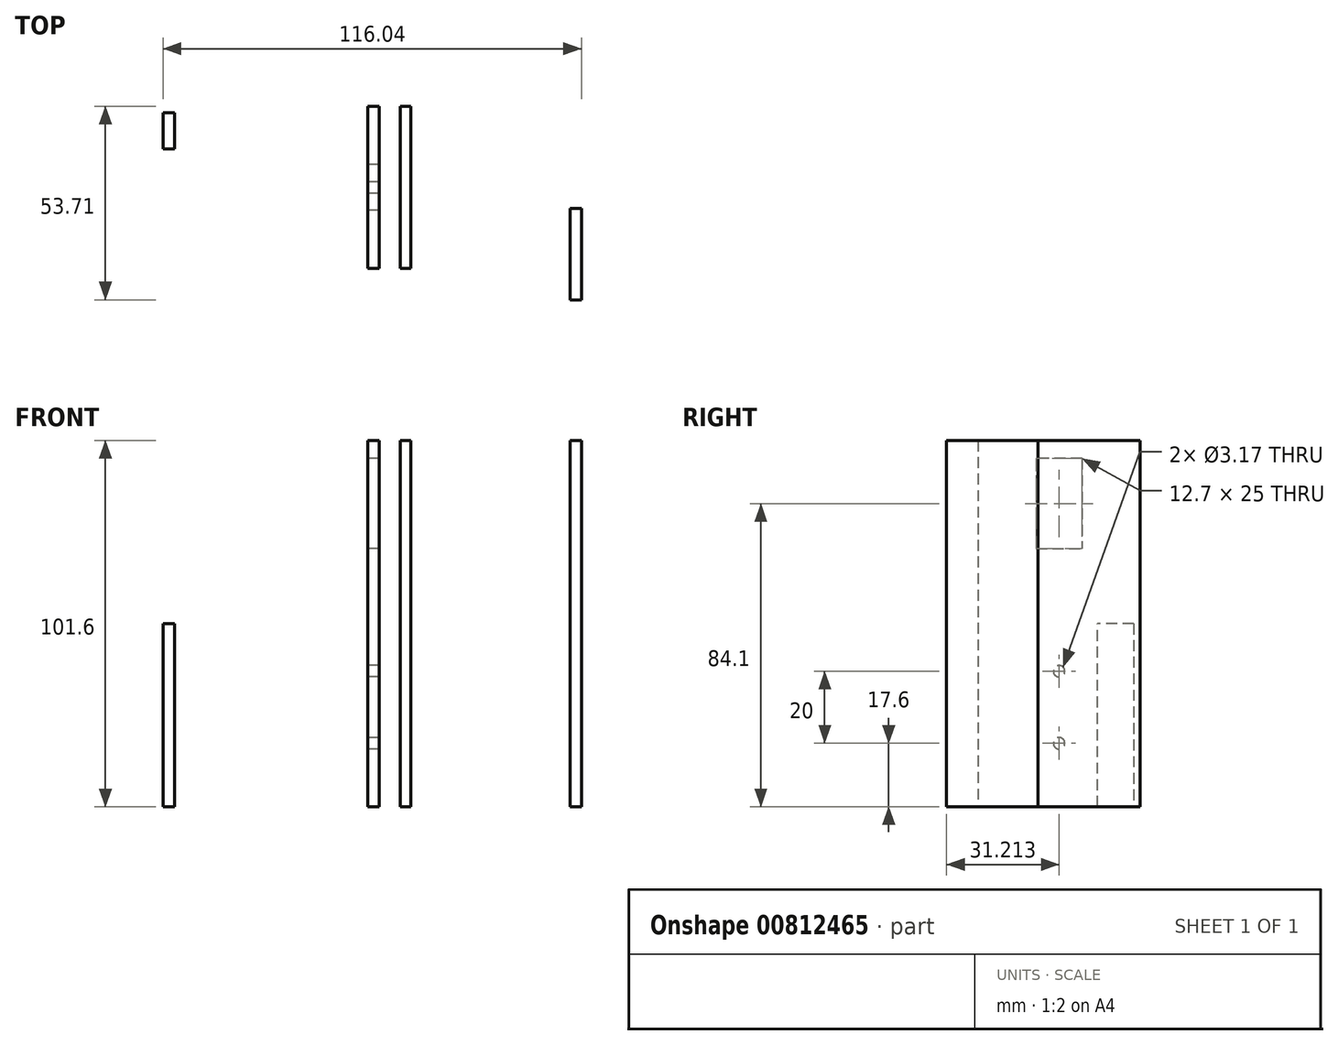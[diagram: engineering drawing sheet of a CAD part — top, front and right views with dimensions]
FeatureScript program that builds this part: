
annotation { "Feature Type Name" : "Feature", "Feature Type Description" : "" }
export const myFeature = defineFeature(function(context is Context, id is Id, definition is map)
    precondition{}
    {
        {
            var Q0;
            Q0=qCreatedBy(makeId("Top.planeOp"),FACE);
            var sketch = newSketch(context, id + "F0", { "sketchPlane" : qUnion([Q0])});
            skLineSegment(sketch, "E0.bottom", {"start": v(-7.16, 39.12) * mm, "end": v(-3.99, 39.12) * mm});
            skLineSegment(sketch, "E0.top", {"start": v(-7.16, -5.88) * mm, "end": v(-3.99, -5.88) * mm});
            skLineSegment(sketch, "E0.left", {"start": v(-7.16, 39.12) * mm, "end": v(-7.16, -5.88) * mm});
            skLineSegment(sketch, "E0.right", {"start": v(-3.99, 39.12) * mm, "end": v(-3.99, -5.88) * mm});
            skLineSegment(sketch, "E1.bottom", {"start": v(1.92, 39.12) * mm, "end": v(4.75, 39.12) * mm});
            skLineSegment(sketch, "E1.top", {"start": v(1.92, -5.88) * mm, "end": v(4.75, -5.88) * mm});
            skLineSegment(sketch, "E1.left", {"start": v(1.92, 39.12) * mm, "end": v(1.92, -5.88) * mm});
            skLineSegment(sketch, "E1.right", {"start": v(4.75, 39.12) * mm, "end": v(4.75, -5.88) * mm});
            skLineSegment(sketch, "E2", {"start": v(-63.9, 37.32) * mm, "end": v(-60.73, 37.32) * mm});
            skLineSegment(sketch, "E3", {"start": v(-60.73, 37.32) * mm, "end": v(-60.73, 17.32) * mm});
            skLineSegment(sketch, "E4.bottom", {"start": v(-60.73, 37.32) * mm, "end": v(-63.9, 37.32) * mm});
            skLineSegment(sketch, "E4.top", {"start": v(-60.73, 17.32) * mm, "end": v(-63.9, 17.32) * mm});
            skLineSegment(sketch, "E4.right", {"start": v(-63.9, 37.32) * mm, "end": v(-63.9, 17.32) * mm});
            skLineSegment(sketch, "E5", {"start": v(-62.32, 37.32) * mm, "end": v(-62.32, 17.32) * mm});
            skLineSegment(sketch, "E6", {"start": v(-63.9, 37.32) * mm, "end": v(-63.9, 27.32) * mm});
            skLineSegment(sketch, "E7.bottom", {"start": v(48.96, 10.81) * mm, "end": v(52.13, 10.81) * mm});
            skLineSegment(sketch, "E7.top", {"start": v(48.96, -14.59) * mm, "end": v(52.13, -14.59) * mm});
            skLineSegment(sketch, "E7.left", {"start": v(48.96, 10.81) * mm, "end": v(48.96, -14.59) * mm});
            skLineSegment(sketch, "E7.right", {"start": v(52.13, 10.81) * mm, "end": v(52.13, -14.59) * mm});
            skSolve(sketch);
        }
        {
            var Q0;
            Q0=makeQuery(id+"F0.imprint","IMPRINT",FACE,{"disambiguationData":[TD([[makeQuery(id+"F0.imprint","IMPRINT",EDGE,{"derivedFrom":sQuery(id+"F0.wireOp",EDGE,"E1.bottom")}),-1.0]])]});
            var Q1;
            Q1=makeQuery(id+"F0.imprint","IMPRINT",FACE,{"disambiguationData":[TD([[makeQuery(id+"F0.imprint","IMPRINT",EDGE,{"derivedFrom":sQuery(id+"F0.wireOp",EDGE,"E0.bottom")}),-1.0]])]});
            var Q2;
            {var subQ0=sQuery(id+"F0.wireOp",EDGE,"E3");Q2=makeQuery(id+"F0.imprint","IMPRINT",FACE,{"disambiguationData":[TD([[makeQuery(id+"F0.imprint","IMPRINT",EDGE,{"derivedFrom":subQ0}),-1.0]])]});}
            var Q3;
            {var subQ0=sQuery(id+"F0.wireOp",EDGE,"E4.right");Q3=makeQuery(id+"F0.imprint","IMPRINT",FACE,{"disambiguationData":[TD([[makeQuery(id+"F0.imprint","IMPRINT",EDGE,{"derivedFrom":subQ0}),1.0]])]});}
            extrude(context, id + "F1", {"entities" : qUnion([Q0, Q1, Q2, Q3]), "depth" : 101.6 * mm, "offsetDistance" : 25.4 * mm});
        }
        {
            var Q0;
            Q0=makeQuery(id+"F1.opExtrude","SWEPT_FACE",FACE,{"disambiguationData":[OSD([sQuery(id+"F0.wireOp",EDGE,"E0.left")])]});
            var sketch = newSketch(context, id + "F2", { "sketchPlane" : qUnion([Q0])});
            skLineSegment(sketch, "E8", {"start": v(5.88, 101.6) * mm, "end": v(-16.62, 101.6) * mm});
            skLineSegment(sketch, "E9", {"start": v(-16.62, 101.6) * mm, "end": v(-39.12, 101.6) * mm});
            skLineSegment(sketch, "E10", {"start": v(-16.62, 101.6) * mm, "end": v(-16.62, 96.6) * mm});
            skLineSegment(sketch, "E11", {"start": v(-16.62, 96.6) * mm, "end": v(-10.27, 96.6) * mm});
            skLineSegment(sketch, "E12", {"start": v(-16.62, 96.6) * mm, "end": v(-22.97, 96.6) * mm});
            skLineSegment(sketch, "E13", {"start": v(-16.62, 71.6) * mm, "end": v(-22.97, 71.6) * mm});
            skLineSegment(sketch, "E14", {"start": v(-16.62, 71.6) * mm, "end": v(-10.27, 71.6) * mm});
            skLineSegment(sketch, "E15", {"start": v(-10.27, 96.6) * mm, "end": v(-10.27, 71.6) * mm});
            skLineSegment(sketch, "E16", {"start": v(-22.97, 96.6) * mm, "end": v(-22.97, 71.6) * mm});
            skPoint(sketch, "E17", {"position": v(-14.12, 84.1) * mm});
            skLineSegment(sketch, "E18", {"start": v(-16.62, 96.6) * mm, "end": v(-16.62, 77.6) * mm});
            skCircle(sketch, "E19", {"center": v(-16.62, 77.6) * mm, "radius": 22.5 * mm});
            skLineSegment(sketch, "E20", {"start": v(-16.62, 55.1) * mm, "end": v(-16.62, 37.6) * mm});
            skLineSegment(sketch, "E21", {"start": v(-16.62, 37.6) * mm, "end": v(-16.62, 20.1) * mm});
            skCircle(sketch, "E22", {"center": v(-16.62, 37.6) * mm, "radius": 17.5 * mm});
            skCircle(sketch, "E23", {"center": v(-16.62, 37.6) * mm, "radius": 12.5 * mm});
            skLineSegment(sketch, "E24", {"start": v(-16.62, 25.1) * mm, "end": v(-16.62, 17.6) * mm});
            skLineSegment(sketch, "E25", {"start": v(-16.62, 17.6) * mm, "end": v(-16.62, 10.1) * mm});
            skCircle(sketch, "E26", {"center": v(-16.62, 17.6) * mm, "radius": 7.5 * mm});
            skCircle(sketch, "E27", {"center": v(-16.62, 37.6) * mm, "radius": 1.59 * mm});
            skCircle(sketch, "E28", {"center": v(-16.62, 17.6) * mm, "radius": 1.59 * mm});
            skSolve(sketch);
        }
        {
            var Q0;
            Q0=makeQuery(id+"F2.imprint","IMPRINT",FACE,{"disambiguationData":[TD([[makeQuery(id+"F2.imprint","IMPRINT",EDGE,{"derivedFrom":sQuery(id+"F2.wireOp",EDGE,"E11")}),-1.0]])]});
            var Q1;
            {var subQ0=sQuery(id+"F2.wireOp",EDGE,"E21");var subQ1=sQuery(id+"F2.wireOp",EDGE,"E20");var subQ2=makeQuery(id+"F2.imprint","INTERSECT",VERTEX,{"derivedFrom":[subQ1,subQ0]});Q1=makeQuery(id+"F2.imprint","IMPRINT",FACE,{"disambiguationData":[TD([[makeQuery(id+"F2.imprint","IMPRINT",EDGE,{"disambiguationData":[TD([[subQ2,1.0]])],"derivedFrom":subQ1}),-1.0]])]});}
            var Q2;
            {var subQ0=sQuery(id+"F2.wireOp",EDGE,"E21");var subQ1=sQuery(id+"F2.wireOp",EDGE,"E20");var subQ2=makeQuery(id+"F2.imprint","INTERSECT",VERTEX,{"derivedFrom":[subQ1,subQ0]});Q2=makeQuery(id+"F2.imprint","IMPRINT",FACE,{"disambiguationData":[TD([[makeQuery(id+"F2.imprint","IMPRINT",EDGE,{"disambiguationData":[TD([[subQ2,1.0]])],"derivedFrom":subQ1}),1.0]])]});}
            var Q3;
            {var subQ0=sQuery(id+"F2.wireOp",EDGE,"E25");var subQ1=sQuery(id+"F2.wireOp",EDGE,"E24");var subQ2=makeQuery(id+"F2.imprint","INTERSECT",VERTEX,{"derivedFrom":[subQ1,subQ0]});Q3=makeQuery(id+"F2.imprint","IMPRINT",FACE,{"disambiguationData":[TD([[makeQuery(id+"F2.imprint","IMPRINT",EDGE,{"disambiguationData":[TD([[subQ2,1.0]])],"derivedFrom":subQ1}),1.0]])]});}
            var Q4;
            {var subQ0=sQuery(id+"F2.wireOp",EDGE,"E25");var subQ1=sQuery(id+"F2.wireOp",EDGE,"E24");var subQ2=makeQuery(id+"F2.imprint","INTERSECT",VERTEX,{"derivedFrom":[subQ1,subQ0]});Q4=makeQuery(id+"F2.imprint","IMPRINT",FACE,{"disambiguationData":[TD([[makeQuery(id+"F2.imprint","IMPRINT",EDGE,{"disambiguationData":[TD([[subQ2,1.0]])],"derivedFrom":subQ1}),-1.0]])]});}
            extrude(context, id + "F3", {"entities" : qUnion([Q0, Q1, Q2, Q3, Q4]), "operationType" : NewBodyOperationType.REMOVE, "oppositeDirection" : true, "depth" : 3.17 * mm, "offsetDistance" : 25.4 * mm});
        }
        {
            var Q0;
            Q0=makeQuery(id+"F1.opExtrude","CAP_FACE",FACE,{"disambiguationData":[OSD([sQuery(id+"F0.wireOp",EDGE,"E4.bottom"),sQuery(id+"F0.wireOp",EDGE,"E4.top"),sQuery(id+"F0.wireOp",EDGE,"E3"),sQuery(id+"F0.wireOp",EDGE,"E4.right"),sQuery(id+"F0.wireOp",EDGE,"E6"),sQuery(id+"F0.wireOp",EDGE,"oetj8XLk-KtwH-fAax-UgUl-eVdQMSs61eWB")])],"isStart":false});
            extrude(context, id + "F4", {"entities" : qUnion([Q0]), "operationType" : NewBodyOperationType.REMOVE, "oppositeDirection" : true, "depth" : 50.8 * mm, "offsetDistance" : 25.4 * mm});
        }
        {
            var Q0;
            Q0=makeQuery(id+"F1.opExtrude","SWEPT_FACE",FACE,{"disambiguationData":[OSD([sQuery(id+"F0.wireOp",EDGE,"E4.right"),sQuery(id+"F0.wireOp",EDGE,"E6")])]});
            var sketch = newSketch(context, id + "F5", { "sketchPlane" : qUnion([Q0])});
            skLineSegment(sketch, "E29", {"start": v(-37.32, 0) * mm, "end": v(-37.32, 50.8) * mm});
            skLineSegment(sketch, "E30", {"start": v(-37.32, 0) * mm, "end": v(-37.32, 25.4) * mm});
            skLineSegment(sketch, "E31", {"start": v(-37.32, 25.4) * mm, "end": v(-17.32, 25.4) * mm});
            skLineSegment(sketch, "E32", {"start": v(-37.32, 0) * mm, "end": v(-17.32, 0) * mm});
            skLineSegment(sketch, "E33", {"start": v(-37.32, 0) * mm, "end": v(-27.32, 0) * mm});
            skLineSegment(sketch, "E34", {"start": v(-27.32, 0) * mm, "end": v(-27.32, 50.8) * mm});
            skCircle(sketch, "E35", {"center": v(-27.32, 25.4) * mm, "radius": 1.59 * mm});
            skSolve(sketch);
        }
        {
            var Q0;
            {var subQ0=sQuery(id+"F5.wireOp",EDGE,"E34");var subQ1=sQuery(id+"F5.wireOp",EDGE,"E31");var subQ2=makeQuery(id+"F5.imprint","INTERSECT",VERTEX,{"derivedFrom":[subQ1,subQ0]});Q0=makeQuery(id+"F5.imprint","IMPRINT",FACE,{"disambiguationData":[TD([[makeQuery(id+"F5.imprint","IMPRINT",EDGE,{"disambiguationData":[TD([[subQ2,-1.0]])],"derivedFrom":subQ1}),1.0]])]});}
            var Q1;
            {var subQ0=sQuery(id+"F5.wireOp",EDGE,"E35");var subQ1=sQuery(id+"F5.wireOp",EDGE,"E31");var subQ2=makeQuery(id+"F5.imprint","INTERSECT",VERTEX,{"disambiguationData":[OD(0.0)],"derivedFrom":[subQ1,subQ0]});Q1=makeQuery(id+"F5.imprint","IMPRINT",FACE,{"disambiguationData":[TD([[makeQuery(id+"F5.imprint","IMPRINT",EDGE,{"disambiguationData":[TD([[subQ2,-1.0]])],"derivedFrom":subQ1}),1.0]])]});}
            var Q2;
            {var subQ0=sQuery(id+"F5.wireOp",EDGE,"E35");var subQ1=sQuery(id+"F5.wireOp",EDGE,"E31");var subQ2=makeQuery(id+"F5.imprint","INTERSECT",VERTEX,{"disambiguationData":[OD(0.0)],"derivedFrom":[subQ1,subQ0]});Q2=makeQuery(id+"F5.imprint","IMPRINT",FACE,{"disambiguationData":[TD([[makeQuery(id+"F5.imprint","IMPRINT",EDGE,{"disambiguationData":[TD([[subQ2,-1.0]])],"derivedFrom":subQ1}),-1.0]])]});}
            var Q3;
            {var subQ0=sQuery(id+"F5.wireOp",EDGE,"E34");var subQ1=sQuery(id+"F5.wireOp",EDGE,"E31");var subQ2=makeQuery(id+"F5.imprint","INTERSECT",VERTEX,{"derivedFrom":[subQ1,subQ0]});Q3=makeQuery(id+"F5.imprint","IMPRINT",FACE,{"disambiguationData":[TD([[makeQuery(id+"F5.imprint","IMPRINT",EDGE,{"disambiguationData":[TD([[subQ2,-1.0]])],"derivedFrom":subQ1}),-1.0]])]});}
            extrude(context, id + "F6", {"entities" : qUnion([Q0, Q1, Q2, Q3]), "operationType" : NewBodyOperationType.REMOVE, "oppositeDirection" : true, "depth" : 3.17 * mm, "offsetDistance" : 25.4 * mm});
        }
        {
            var Q0;
            Q0=makeQuery(id+"F0.imprint","IMPRINT",FACE,{"disambiguationData":[TD([[makeQuery(id+"F0.imprint","IMPRINT",EDGE,{"derivedFrom":sQuery(id+"F0.wireOp",EDGE,"E7.bottom")}),-1.0]])]});
            extrude(context, id + "F7", {"entities" : qUnion([Q0]), "depth" : 101.6 * mm, "offsetDistance" : 25.4 * mm});
        }
    });
